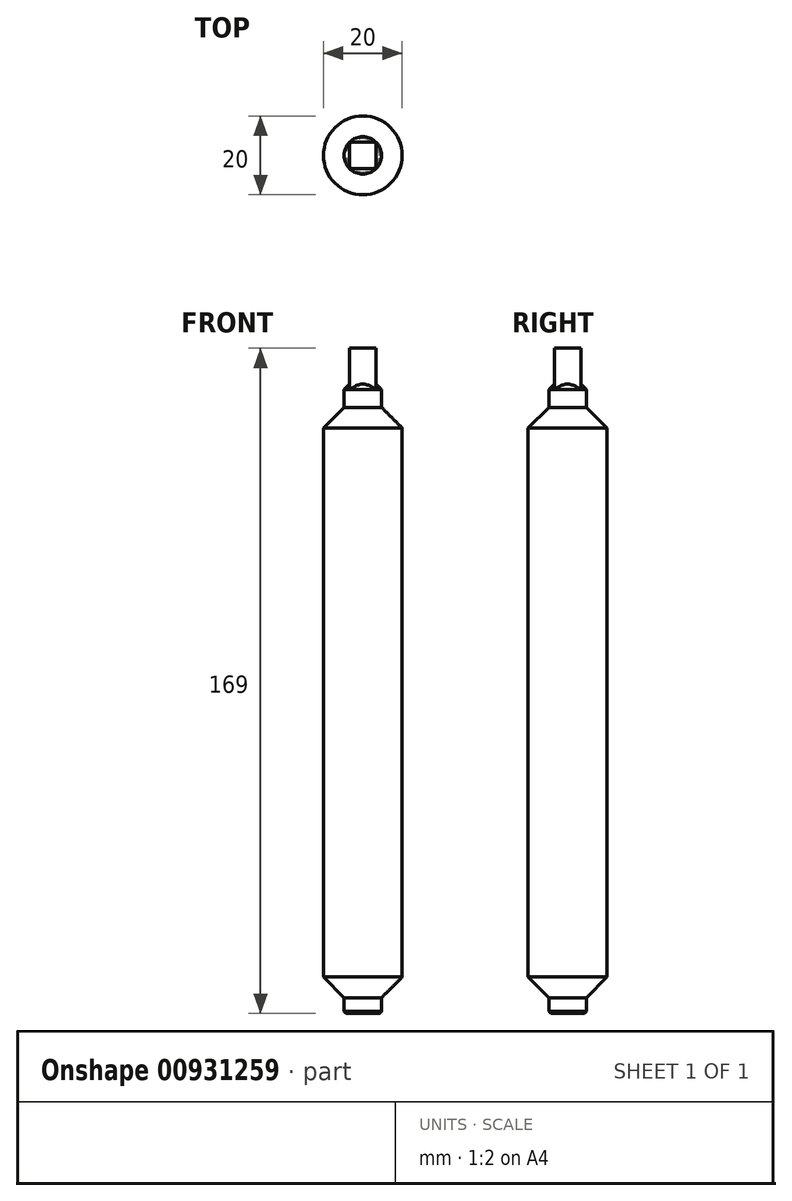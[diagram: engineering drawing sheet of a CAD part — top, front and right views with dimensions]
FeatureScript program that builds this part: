
annotation { "Feature Type Name" : "Feature", "Feature Type Description" : "" }
export const myFeature = defineFeature(function(context is Context, id is Id, definition is map)
    precondition{}
    {
        {
            var Q0;
            Q0=qCreatedBy(makeId("Front.planeOp"),FACE);
            var sketch = newSketch(context, id + "F0", { "sketchPlane" : qUnion([Q0])});
            skLineSegment(sketch, "E0", {"start": v(0, -80) * mm, "end": v(4.75, -80) * mm});
            skLineSegment(sketch, "E1", {"start": v(4.75, -80) * mm, "end": v(4.75, -76) * mm});
            skLineSegment(sketch, "E2", {"start": v(4.75, -76) * mm, "end": v(10, -70.75) * mm});
            skLineSegment(sketch, "E3", {"start": v(10, -70.75) * mm, "end": v(10, 68.75) * mm});
            skLineSegment(sketch, "E4", {"start": v(10, 68.75) * mm, "end": v(4.75, 74) * mm});
            skLineSegment(sketch, "E5", {"start": v(4.75, 74) * mm, "end": v(4.75, 80) * mm});
            skLineSegment(sketch, "E6", {"start": v(4.75, 80) * mm, "end": v(0, 80) * mm});
            skLineSegment(sketch, "E7", {"start": v(0, 80) * mm, "end": v(0, -80) * mm});
            skSolve(sketch);
        }
        {
            var Q0;
            Q0 = qSketchRegion(id + "F0", true);
            var Q1;
            Q1=sQuery(id+"F0.wireOp",EDGE,"E7");
            revolve(context, id + "F1", {"surfaceOperationType" : NewSurfaceOperationType.NEW, "entities" : qUnion([Q0]), "axis" : qUnion([Q1]), "revolveType" : RevolveType.FULL});
        }
        {
            var Q0;
            Q0=makeQuery(id+"F1.opRevolve","SWEPT_EDGE",EDGE,{"disambiguationData":[OSD([sQuery(id+"F0.wireOp",EDGE,"E5"),sQuery(id+"F0.wireOp",EDGE,"E6")])]});
            chamfer(context, id + "F2", {"entities" : qUnion([Q0]), "width" : 1.5 * mm, "tangentPropagation" : true});
        }
        {
            var Q0;
            Q0=makeQuery(id+"F1.opRevolve","SWEPT_FACE",FACE,{"disambiguationData":[OSD([sQuery(id+"F0.wireOp",EDGE,"E6")])]});
            var sketch = newSketch(context, id + "F3", { "sketchPlane" : qUnion([Q0])});
            skLineSegment(sketch, "E8.bottom", {"start": v(3.36, 3.36) * mm, "end": v(-3.36, 3.36) * mm});
            skLineSegment(sketch, "E8.top", {"start": v(3.36, -3.36) * mm, "end": v(-3.36, -3.36) * mm});
            skLineSegment(sketch, "E8.left", {"start": v(3.36, 3.36) * mm, "end": v(3.36, -3.36) * mm});
            skLineSegment(sketch, "E8.right", {"start": v(-3.36, 3.36) * mm, "end": v(-3.36, -3.36) * mm});
            skPoint(sketch, "E8.middle", {"position": v(0, 0) * mm});
            skCircle(sketch, "E9.0", {"center": v(0, 0) * mm, "radius": 4.75 * mm, "construction": true});
            skSolve(sketch);
        }
        {
            var Q0;
            Q0 = qSketchRegion(id + "F3", true);
            extrude(context, id + "F4", {"entities" : qUnion([Q0]), "operationType" : NewBodyOperationType.ADD, "depth" : 9 * mm, "offsetDistance" : 25 * mm, "hasSecondDirection" : true, "secondDirectionOppositeDirection" : true, "secondDirectionDepth" : 3 * mm});
        }
        {
            var Q0;
            Q0=makeQuery(id+"F1.opRevolve","SWEPT_EDGE",EDGE,{"disambiguationData":[OSD([sQuery(id+"F0.wireOp",EDGE,"E0"),sQuery(id+"F0.wireOp",EDGE,"E1")])]});
            chamfer(context, id + "F5", {"entities" : qUnion([Q0]), "width" : 0.5 * mm, "tangentPropagation" : true});
        }
    });
